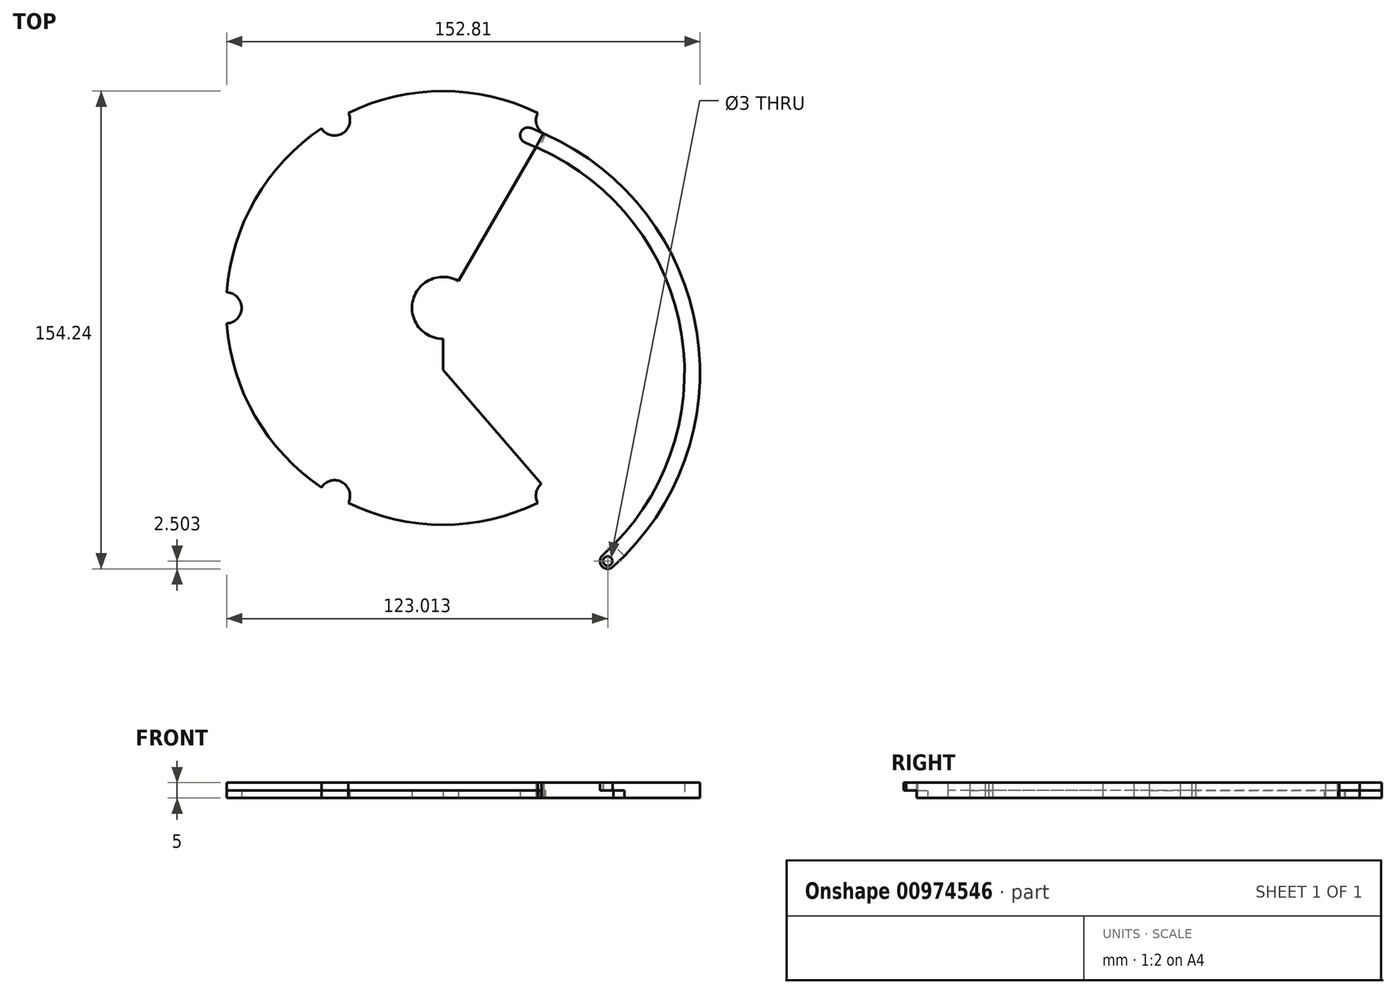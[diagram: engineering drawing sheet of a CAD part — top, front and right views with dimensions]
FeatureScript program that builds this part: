
annotation { "Feature Type Name" : "Feature", "Feature Type Description" : "" }
export const myFeature = defineFeature(function(context is Context, id is Id, definition is map)
    precondition{}
    {
        {
            var Q0;
            Q0=qCreatedBy(makeId("Top.planeOp"),FACE);
            var sketch = newSketch(context, id + "F0", { "sketchPlane" : qUnion([Q0])});
            skCircle(sketch, "E0", {"center": v(0, 0) * mm, "radius": 100 * mm});
            skCircle(sketch, "E1", {"center": v(0, 0) * mm, "radius": 70 * mm});
            skCircle(sketch, "E2", {"center": v(0, 0) * mm, "radius": 10 * mm});
            skLineSegment(sketch, "E3", {"start": v(0, 0) * mm, "end": v(70, 0) * mm});
            skLineSegment(sketch, "E4", {"start": v(70, 0) * mm, "end": v(100, 0) * mm});
            skLineSegment(sketch, "E5.bottom", {"start": v(70, 0) * mm, "end": v(75, 0) * mm});
            skCircle(sketch, "E6.1.0", {"center": v(35, 60.62) * mm, "radius": 5 * mm});
            skCircle(sketch, "E6.2.0", {"center": v(-35, 60.62) * mm, "radius": 5 * mm});
            skCircle(sketch, "E6.3.0", {"center": v(-70, 0) * mm, "radius": 5 * mm});
            skCircle(sketch, "E6.4.0", {"center": v(-35, -60.62) * mm, "radius": 5 * mm});
            skCircle(sketch, "E6.5.0", {"center": v(35, -60.62) * mm, "radius": 5 * mm});
            skLineSegment(sketch, "E7", {"start": v(0, 0) * mm, "end": v(35, 60.62) * mm});
            skLineSegment(sketch, "E8", {"start": v(0, 0) * mm, "end": v(35, -60.62) * mm});
            skLineSegment(sketch, "E9", {"start": v(0, 0) * mm, "end": v(50, -86.6) * mm});
            skPoint(sketch, "E10", {"position": v(50, -86.6) * mm});
            skLineSegment(sketch, "E11", {"start": v(32.5, 56.3) * mm, "end": v(30, 51.96) * mm});
            skLineSegment(sketch, "E12", {"start": v(75, 0) * mm, "end": v(82.57, 0) * mm});
            skLineSegment(sketch, "E13", {"start": v(0, 0) * mm, "end": v(0, -20) * mm});
            skLineSegment(sketch, "E14", {"start": v(0, -20) * mm, "end": v(35, -60.62) * mm});
            skPoint(sketch, "E15", {"position": v(54.83, -83.63) * mm});
            skPoint(sketch, "E16", {"position": v(33, 56.04) * mm});
            skLineSegment(sketch, "E17", {"start": v(33, 56.04) * mm, "end": v(31.02, 51.45) * mm});
            skArc(sketch, "E18", {"start": v(51.56, -79.84) * mm, "mid": v(77.04, -8.6) * mm, "end": v(31.02, 51.45) * mm});
            skArc(sketch, "E19", {"start": v(54.83, -83.63) * mm, "mid": v(81.98, -7.85) * mm, "end": v(33, 56.04) * mm});
            skLineSegment(sketch, "E20", {"start": v(33, 56.04) * mm, "end": v(28.42, 58.03) * mm});
            skLineSegment(sketch, "E21", {"start": v(31.02, 51.45) * mm, "end": v(26.43, 53.44) * mm});
            skArc(sketch, "E22", {"start": v(51.56, -79.84) * mm, "mid": v(51.3, -83.37) * mm, "end": v(54.83, -83.63) * mm});
            skCircle(sketch, "E23", {"center": v(53.2, -81.74) * mm, "radius": 1.5 * mm});
            skArc(sketch, "E24", {"start": v(26.43, 53.44) * mm, "mid": v(25.13, 56.73) * mm, "end": v(28.42, 58.03) * mm});
            skCircle(sketch, "E25", {"center": v(27.43, 55.73) * mm, "radius": 1.5 * mm});
            skPoint(sketch, "E26", {"position": v(25.13, 56.73) * mm});
            skPoint(sketch, "E27", {"position": v(32.01, 53.74) * mm});
            skPoint(sketch, "E28", {"position": v(51.3, -83.37) * mm});
            skLineSegment(sketch, "E29", {"start": v(58.56, -80.1) * mm, "end": v(55.07, -76.51) * mm});
            skSolve(sketch);
        }
        {
            var Q0;
            {var subQ0=sQuery(id+"F0.wireOp",EDGE,"E24");Q0=makeQuery(id+"F0.imprint","IMPRINT",FACE,{"disambiguationData":[TD([[makeQuery(id+"F0.imprint","IMPRINT",EDGE,{"derivedFrom":subQ0}),-1.0]])]});}
            var Q1;
            {var subQ5=sQuery(id+"F0.wireOp",EDGE,"E17");Q1=makeQuery(id+"F0.imprint","IMPRINT",FACE,{"disambiguationData":[TD([[makeQuery(id+"F0.imprint","IMPRINT",EDGE,{"derivedFrom":subQ5}),1.0]])]});}
            var Q2;
            {var subQ1=sQuery(id+"F0.wireOp",EDGE,"E17");Q2=makeQuery(id+"F0.imprint","IMPRINT",FACE,{"disambiguationData":[TD([[makeQuery(id+"F0.imprint","IMPRINT",EDGE,{"derivedFrom":subQ1}),-1.0]])]});}
            var Q3;
            {var subQ5=sQuery(id+"F0.wireOp",EDGE,"i9XkPh53-tHNP-yqC6-lyee-TFpcAWpolQF8");Q3=makeQuery(id+"F0.imprint","IMPRINT",FACE,{"disambiguationData":[TD([[makeQuery(id+"F0.imprint","IMPRINT",EDGE,{"derivedFrom":subQ5}),1.0]])]});}
            var Q4;
            Q4=makeQuery(id+"F0.imprint","IMPRINT",FACE,{"disambiguationData":[TD([[makeQuery(id+"F0.imprint","IMPRINT",EDGE,{"derivedFrom":sQuery(id+"F0.wireOp",EDGE,"E23")}),-1.0]])]});
            var Q5;
            {var subQ5=sQuery(id+"F0.wireOp",EDGE,"i9XkPh53-tHNP-yqC6-lyee-TFpcAWpolQF8");Q5=makeQuery(id+"F0.imprint","IMPRINT",FACE,{"disambiguationData":[TD([[makeQuery(id+"F0.imprint","IMPRINT",EDGE,{"derivedFrom":subQ5}),-1.0]])]});}
            var Q6;
            {var subQ5=sQuery(id+"F0.wireOp",EDGE,"E29");Q6=makeQuery(id+"F0.imprint","IMPRINT",FACE,{"disambiguationData":[TD([[makeQuery(id+"F0.imprint","IMPRINT",EDGE,{"derivedFrom":subQ5}),-1.0]])]});}
            var Q7;
            {var subQ0=sQuery(id+"F0.wireOp",EDGE,"E22");var subQ1=sQuery(id+"F0.wireOp",EDGE,"E0");var subQ3=makeQuery(id+"F0.imprint","INTERSECT",VERTEX,{"derivedFrom":[subQ1,subQ0]});Q7=makeQuery(id+"F0.imprint","IMPRINT",FACE,{"disambiguationData":[TD([[makeQuery(id+"F0.imprint","IMPRINT",EDGE,{"disambiguationData":[TD([[subQ3,-1.0]])],"derivedFrom":subQ1}),-1.0]])]});}
            var Q8;
            {var subQ0=sQuery(id+"F0.wireOp",EDGE,"E18");var subQ1=sQuery(id+"F0.wireOp",EDGE,"E1");var subQ2=makeQuery(id+"F0.imprint","INTERSECT",VERTEX,{"derivedFrom":[subQ1,subQ0]});Q8=makeQuery(id+"F0.imprint","IMPRINT",FACE,{"disambiguationData":[TD([[makeQuery(id+"F0.imprint","IMPRINT",EDGE,{"disambiguationData":[TD([[subQ2,-1.0]])],"derivedFrom":subQ1}),-1.0]])]});}
            extrude(context, id + "F1", {"entities" : qUnion([Q0, Q1, Q2, Q3, Q4, Q5, Q6, Q7, Q8]), "depth" : 5 * mm, "offsetDistance" : 25 * mm});
        }
        {
            var Q0;
            {var subQ1=sQuery(id+"F0.wireOp",EDGE,"E17");Q0=makeQuery(id+"F0.imprint","IMPRINT",FACE,{"disambiguationData":[TD([[makeQuery(id+"F0.imprint","IMPRINT",EDGE,{"derivedFrom":subQ1}),-1.0]])]});}
            var Q1;
            {var subQ0=sQuery(id+"F0.wireOp",EDGE,"E24");Q1=makeQuery(id+"F0.imprint","IMPRINT",FACE,{"disambiguationData":[TD([[makeQuery(id+"F0.imprint","IMPRINT",EDGE,{"derivedFrom":subQ0}),-1.0]])]});}
            extrude(context, id + "F2", {"entities" : qUnion([Q0, Q1]), "oppositeDirection" : true, "depth" : -2.5 * mm, "offsetDistance" : 25 * mm});
        }
        {
            var Q0;
            Q0=makeQuery(id+"F2.opExtrude","SWEPT_BODY",BODY,{"disambiguationData":[OSD([sQuery(id+"F0.wireOp",EDGE,"E17"),sQuery(id+"F0.wireOp",EDGE,"E20"),sQuery(id+"F0.wireOp",EDGE,"E21"),sQuery(id+"F0.wireOp",EDGE,"E24"),sQuery(id+"F0.wireOp",EDGE,"E25")])]});
            var Q1;
            Q1=makeQuery(id+"F1.opExtrude","SWEPT_BODY",BODY,{"disambiguationData":[OSD([sQuery(id+"F0.wireOp",EDGE,"E0"),sQuery(id+"F0.wireOp",EDGE,"4bDspzHD-0bnf-D901-04v6-hGpizJ2NbvlH"),sQuery(id+"F0.wireOp",EDGE,"E18"),sQuery(id+"F0.wireOp",EDGE,"E19"),sQuery(id+"F0.wireOp",EDGE,"E20"),sQuery(id+"F0.wireOp",EDGE,"E21"),sQuery(id+"F0.wireOp",EDGE,"E22"),sQuery(id+"F0.wireOp",EDGE,"E23"),sQuery(id+"F0.wireOp",EDGE,"E24"),sQuery(id+"F0.wireOp",EDGE,"E25")])]});
            booleanBodies(context, id + "F3", {"operationType" : BooleanOperationType.SUBTRACTION, "tools" : qUnion([Q0]), "targets" : qUnion([Q1])});
        }
        {
            var Q0;
            Q0=makeQuery(id+"F0.imprint","IMPRINT",FACE,{"disambiguationData":[TD([[makeQuery(id+"F0.imprint","IMPRINT",EDGE,{"derivedFrom":sQuery(id+"F0.wireOp",EDGE,"E23")}),-1.0]])]});
            var Q1;
            {var subQ0=sQuery(id+"F0.wireOp",EDGE,"E22");var subQ1=sQuery(id+"F0.wireOp",EDGE,"E0");var subQ3=makeQuery(id+"F0.imprint","INTERSECT",VERTEX,{"derivedFrom":[subQ1,subQ0]});Q1=makeQuery(id+"F0.imprint","IMPRINT",FACE,{"disambiguationData":[TD([[makeQuery(id+"F0.imprint","IMPRINT",EDGE,{"disambiguationData":[TD([[subQ3,-1.0]])],"derivedFrom":subQ1}),-1.0]])]});}
            extrude(context, id + "F4", {"entities" : qUnion([Q0, Q1]), "depth" : 2.5 * mm, "offsetDistance" : 25 * mm});
        }
        {
            var Q0;
            Q0=makeQuery(id+"F4.opExtrude","SWEPT_BODY",BODY,{"disambiguationData":[OSD([sQuery(id+"F0.wireOp",EDGE,"E18"),sQuery(id+"F0.wireOp",EDGE,"E19"),sQuery(id+"F0.wireOp",EDGE,"E22"),sQuery(id+"F0.wireOp",EDGE,"E23"),sQuery(id+"F0.wireOp",EDGE,"E29")])]});
            var Q1;
            Q1=makeQuery(id+"F1.opExtrude","SWEPT_BODY",BODY,{"disambiguationData":[OSD([sQuery(id+"F0.wireOp",EDGE,"4bDspzHD-0bnf-D901-04v6-hGpizJ2NbvlH"),sQuery(id+"F0.wireOp",EDGE,"E18"),sQuery(id+"F0.wireOp",EDGE,"E19"),sQuery(id+"F0.wireOp",EDGE,"E20"),sQuery(id+"F0.wireOp",EDGE,"E21"),sQuery(id+"F0.wireOp",EDGE,"E22"),sQuery(id+"F0.wireOp",EDGE,"E23"),sQuery(id+"F0.wireOp",EDGE,"E24"),sQuery(id+"F0.wireOp",EDGE,"E25")])]});
            booleanBodies(context, id + "F5", {"operationType" : BooleanOperationType.SUBTRACTION, "tools" : qUnion([Q0]), "targets" : qUnion([Q1])});
        }
    });
